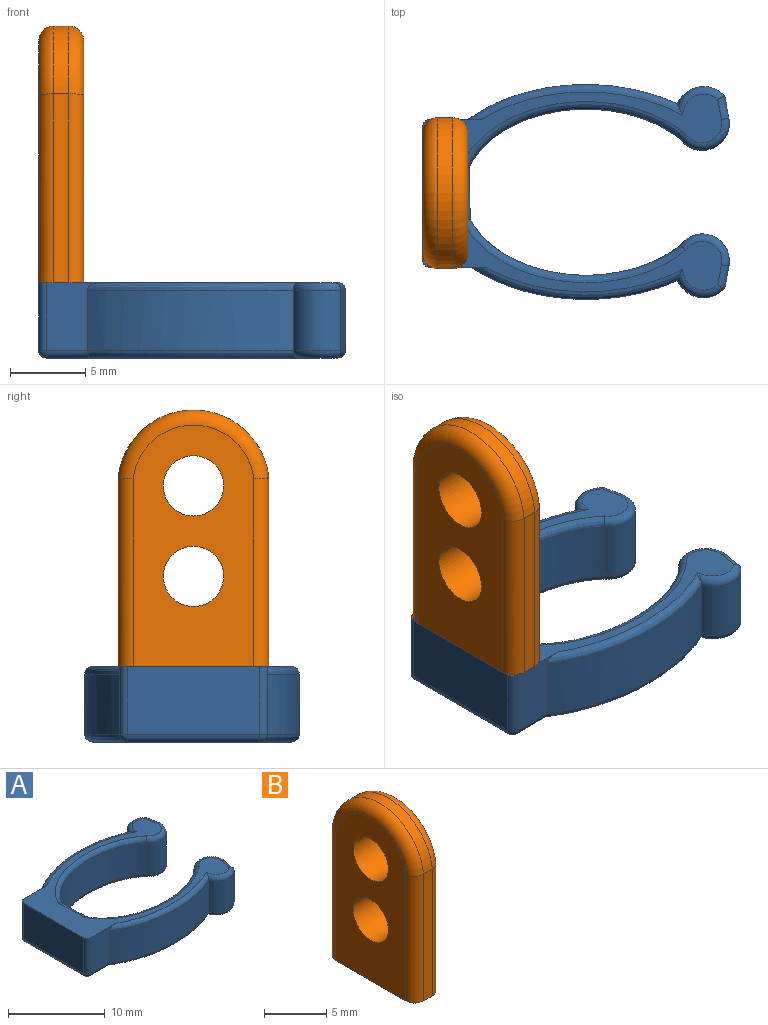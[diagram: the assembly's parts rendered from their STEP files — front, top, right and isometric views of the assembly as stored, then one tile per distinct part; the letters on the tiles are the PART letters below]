
ASSEMBLY  parts=2 mates=1
PART A: 45 faces, bbox 20.8x14.6x5.3 mm
  f0: plane 4x1.47mm, normal (0.98,0.19,0), area 6mm2, adj f1,f13,f18,f35
  f1: cylinder r=1.88mm len=4mm, axis (0,0,-1), area 15.1mm2, adj f0,f2,f17,f38
  f2: extruded ~13.89x4mm, area 58.2mm2, adj f1,f3,f16,f40
  f3: plane 4.76x3.65mm, normal (0,1,0), area 11.3mm2, adj f2,f14,f16,f42,f44
  f4: plane 8.8x4.5mm, normal (-1,0,0), area 39.6mm2, adj f14,f36,f41,f44
  f5: plane 4.77x3.96mm, normal (0,-1,0), area 12.4mm2, adj f6,f14,f22,f36,f37
  f6: extruded ~13.65x4mm, area 56.9mm2, adj f5,f7,f22,f34
  f7: cylinder r=1.88mm len=4mm, axis (0,0,-1), area 15.1mm2, adj f6,f8,f24,f32
  f8: plane 4x1.47mm, normal (0.98,-0.19,0), area 6mm2, adj f7,f9,f26,f30
  f9: cylinder r=1.8mm len=4mm, axis (0,0,-1), area 19.4mm2, adj f8,f10,f25,f28
  f10: extruded ~13.92x4mm, area 62.5mm2, adj f9,f11,f23,f27
  f11: plane 4x3.43mm, normal (1,0.02,0), area 13.7mm2, adj f10,f12,f21,f29
  f12: extruded ~14.01x4mm, area 63.2mm2, adj f11,f13,f20,f31
  f13: cylinder r=1.8mm len=4mm, axis (0,0,-1), area 19.4mm2, adj f0,f12,f19,f33
  f14: plane 19.83x13.24mm, normal (0,0,1), area 65mm2, adj f3,f4,f5,f16,f17,f18,f19,f20
  f15: plane 19.33x13.24mm, normal (0,0,-1), area 57.1mm2, adj f27,f28,f29,f30,f31,f32,f33,f34
  f16: bspline ~15.36x3.11mm, area 11.2mm2, adj f2,f3,f14,f17
  f17: torus R=1.38mm, axis (0,0,1), area 2.9mm2, adj f1,f14,f16,f18
  f18: cylinder r=0.5mm len=1.57mm, axis (0.19,-0.98,0), area 1.1mm2, adj f0,f14,f17,f19
  f19: torus R=1.3mm, axis (0,0,1), area 3.5mm2, adj f13,f14,f18,f20
  f20: bspline ~15.68x4.88mm, area 12.7mm2, adj f12,f14,f19,f21
  f21: cylinder r=0.5mm len=3.66mm, axis (0.02,-1,0), area 2.8mm2, adj f11,f14,f20,f23
  f22: bspline ~15.82x3.09mm, area 11mm2, adj f5,f6,f14,f24
  f23: bspline ~16x5.02mm, area 12.6mm2, adj f10,f14,f21,f25
  f24: torus R=1.38mm, axis (0,0,1), area 2.9mm2, adj f7,f14,f22,f26
  f25: torus R=1.3mm, axis (0,0,1), area 3.5mm2, adj f9,f14,f23,f26
  f26: cylinder r=0.5mm len=1.57mm, axis (-0.19,-0.98,0), area 1.1mm2, adj f8,f14,f24,f25
  f27: bspline ~15.91x4.82mm, area 12.6mm2, adj f10,f15,f28,f29
  f28: torus R=1.3mm, axis (0,0,1), area 3.5mm2, adj f9,f15,f27,f30
  f29: cylinder r=0.5mm len=3.66mm, axis (-0.02,1,0), area 2.8mm2, adj f11,f15,f27,f31
  f30: cylinder r=0.5mm len=1.57mm, axis (0.19,0.98,0), area 1.1mm2, adj f8,f15,f28,f32
  f31: bspline ~15.97x5.06mm, area 12.7mm2, adj f12,f15,f29,f33
  f32: torus R=1.38mm, axis (0,0,1), area 2.9mm2, adj f7,f15,f30,f34
  f33: torus R=1.3mm, axis (0,0,1), area 3.5mm2, adj f13,f15,f31,f35
  f34: bspline ~15.47x2.99mm, area 11.3mm2, adj f6,f15,f32,f37
  f35: cylinder r=0.5mm len=1.57mm, axis (-0.19,0.98,0), area 1.1mm2, adj f0,f15,f33,f38
  f36: cylinder r=0.5mm len=4.5mm, axis (0,0,-1), area 3.5mm2, adj f4,f5,f14,f39
  f37: cylinder r=0.5mm len=2.89mm, axis (1,0,0), area 2.2mm2, adj f5,f15,f34,f39
  f38: torus R=1.38mm, axis (0,0,1), area 2.9mm2, adj f1,f15,f35,f40
  f39: sphere r=0.5mm, area 0.4mm2, adj f36,f37,f41
  f40: bspline ~15.19x3.01mm, area 11.6mm2, adj f2,f15,f38,f42
  f41: cylinder r=0.5mm len=8.8mm, axis (0,-1,0), area 6.9mm2, adj f4,f15,f39,f43
  f42: cylinder r=0.5mm len=2.67mm, axis (-1,0,0), area 2mm2, adj f3,f15,f40,f43
  f43: sphere r=0.5mm, area 0.5mm2, adj f41,f42,f44
  f44: cylinder r=0.5mm len=4.5mm, axis (0,0,1), area 3.5mm2, adj f3,f4,f14,f43
PART B: 14 faces, bbox 3x10.8x17.4 mm
  f0: plane 12.5x1mm, normal (0,-1,0), area 12.5mm2, adj f1,f5,f8,f11
  f1: plane 10x3mm, normal (0,0,-1), area 29.1mm2, adj f0,f2,f6,f7,f8,f10,f11,f13
  f2: plane 12.5x1mm, normal (0,1,0), area 12.5mm2, adj f1,f5,f10,f13
  f3: cylinder r=2mm len=4mm, axis (-1,0,0), area 37.7mm2, adj f6,f7
  f4: cylinder r=2mm len=4mm, axis (-1,0,0), area 37.7mm2, adj f6,f7
  f5: cylinder r=5.03mm len=10mm, axis (-1,0,0), area 14.7mm2, adj f0,f2,f9,f12
  f6: plane 16x8mm, normal (1,0,0), area 96.1mm2, adj f1,f3,f4,f11,f12,f13
  f7: plane 16x8mm, normal (-1,0,0), area 96.1mm2, adj f1,f3,f4,f8,f9,f10
  f8: cylinder r=1mm len=12.5mm, axis (0,0,-1), area 19.6mm2, adj f0,f1,f7,f9
  f9: torus R=4.03mm, axis (1,0,0), area 21.4mm2, adj f5,f7,f8,f10
  f10: cylinder r=1mm len=12.5mm, axis (0,0,1), area 19.6mm2, adj f1,f2,f7,f9
  f11: cylinder r=1mm len=12.5mm, axis (0,0,1), area 19.6mm2, adj f0,f1,f6,f12
  f12: torus R=4.03mm, axis (1,0,0), area 21.4mm2, adj f5,f6,f11,f13
  f13: cylinder r=1mm len=12.5mm, axis (0,0,-1), area 19.6mm2, adj f1,f2,f6,f12
PLACE A t=(6.12,-0.93,-5.17)mm fixed
PLACE B t=(-4.71,-0.51,7.66)mm
MATE fastened B.f7 <-> A.f4  axis (-1,0,0) through (-4.71,-1.01,-0.17)mm
